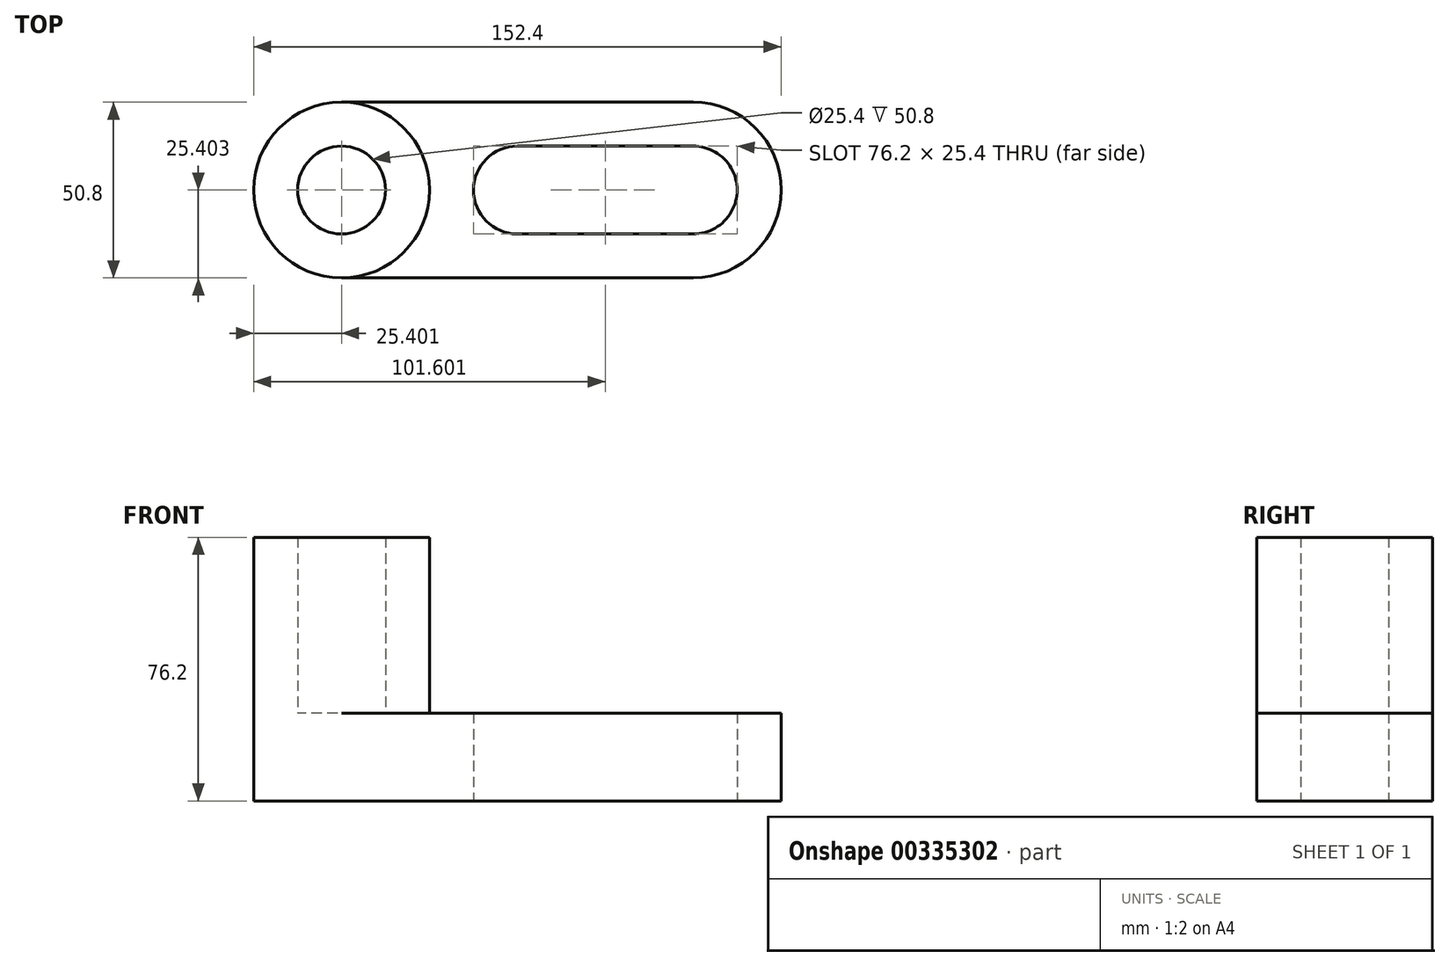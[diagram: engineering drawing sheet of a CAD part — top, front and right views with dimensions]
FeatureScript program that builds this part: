
annotation { "Feature Type Name" : "Feature", "Feature Type Description" : "" }
export const myFeature = defineFeature(function(context is Context, id is Id, definition is map)
    precondition{}
    {
        {
            var Q0;
            Q0=qCreatedBy(makeId("Top.planeOp"),FACE);
            var sketch = newSketch(context, id + "F0", { "sketchPlane" : qUnion([Q0])});
            skLineSegment(sketch, "E0.bottom", {"start": v(-70.6, -43.07) * mm, "end": v(31, -43.07) * mm});
            skLineSegment(sketch, "E0.top", {"start": v(-70.6, 7.73) * mm, "end": v(31, 7.73) * mm});
            skArc(sketch, "E1", {"start": v(31, -43.07) * mm, "mid": v(56.4, -17.67) * mm, "end": v(31, 7.73) * mm});
            skArc(sketch, "E2", {"start": v(31, -30.37) * mm, "mid": v(43.7, -17.67) * mm, "end": v(30.99, -4.97) * mm});
            skArc(sketch, "E3", {"start": v(-19.8, -4.97) * mm, "mid": v(-32.5, -17.67) * mm, "end": v(-19.8, -30.37) * mm});
            skLineSegment(sketch, "E4", {"start": v(-19.8, -4.97) * mm, "end": v(30.99, -4.97) * mm});
            skLineSegment(sketch, "E5", {"start": v(31, -30.37) * mm, "end": v(-19.8, -30.37) * mm});
            skPoint(sketch, "E6.visualSharp", {"position": v(-96, 7.73) * mm});
            skPoint(sketch, "E7.visualSharp", {"position": v(-96, -43.07) * mm});
            skLineSegment(sketch, "E8", {"start": v(-96, -17.67) * mm, "end": v(-96, -17.67) * mm});
            skArc(sketch, "E9.filletArc", {"start": v(-70.6, 7.73) * mm, "mid": v(-88.57, 0.3) * mm, "end": v(-96, -17.67) * mm});
            skArc(sketch, "E10.filletArc", {"start": v(-96, -17.67) * mm, "mid": v(-88.57, -35.63) * mm, "end": v(-70.6, -43.07) * mm});
            skSolve(sketch);
        }
        {
            var Q0;
            Q0=makeQuery(id+"F0.imprint","IMPRINT",FACE,{"disambiguationData":[TD([[makeQuery(id+"F0.imprint","IMPRINT",EDGE,{"derivedFrom":sQuery(id+"F0.wireOp",EDGE,"E0.bottom")}),1.0]])]});
            extrude(context, id + "F1", {"entities" : qUnion([Q0]), "depth" : 25.4 * mm});
        }
        {
            var Q0;
            Q0=makeQuery(id+"F1.opExtrude","CAP_FACE",FACE,{"disambiguationData":[OSD([sQuery(id+"F0.wireOp",EDGE,"E0.bottom"),sQuery(id+"F0.wireOp",EDGE,"E0.top"),sQuery(id+"F0.wireOp",EDGE,"E0.left"),sQuery(id+"F0.wireOp",EDGE,"E1"),sQuery(id+"F0.wireOp",EDGE,"E2"),sQuery(id+"F0.wireOp",EDGE,"E3"),sQuery(id+"F0.wireOp",EDGE,"E4"),sQuery(id+"F0.wireOp",EDGE,"E5"),sQuery(id+"F0.wireOp",EDGE,"E6.filletArc"),sQuery(id+"F0.wireOp",EDGE,"E7.filletArc")])],"isStart":false});
            var sketch = newSketch(context, id + "F2", { "sketchPlane" : qUnion([Q0])});
            skCircle(sketch, "E11", {"center": v(-70.6, -17.67) * mm, "radius": 25.4 * mm});
            skPoint(sketch, "E11.centerSnap0", {"position": v(-96, -17.67) * mm});
            skCircle(sketch, "E12", {"center": v(-70.6, -17.67) * mm, "radius": 12.7 * mm});
            skSolve(sketch);
        }
        {
            var Q0;
            Q0=makeQuery(id+"F2.imprint","IMPRINT",FACE,{"disambiguationData":[TD([[makeQuery(id+"F2.imprint","IMPRINT",EDGE,{"derivedFrom":sQuery(id+"F2.wireOp",EDGE,"E12")}),-1.0]])]});
            extrude(context, id + "F3", {"entities" : qUnion([Q0]), "operationType" : NewBodyOperationType.ADD, "depth" : 50.8 * mm});
        }
    });
